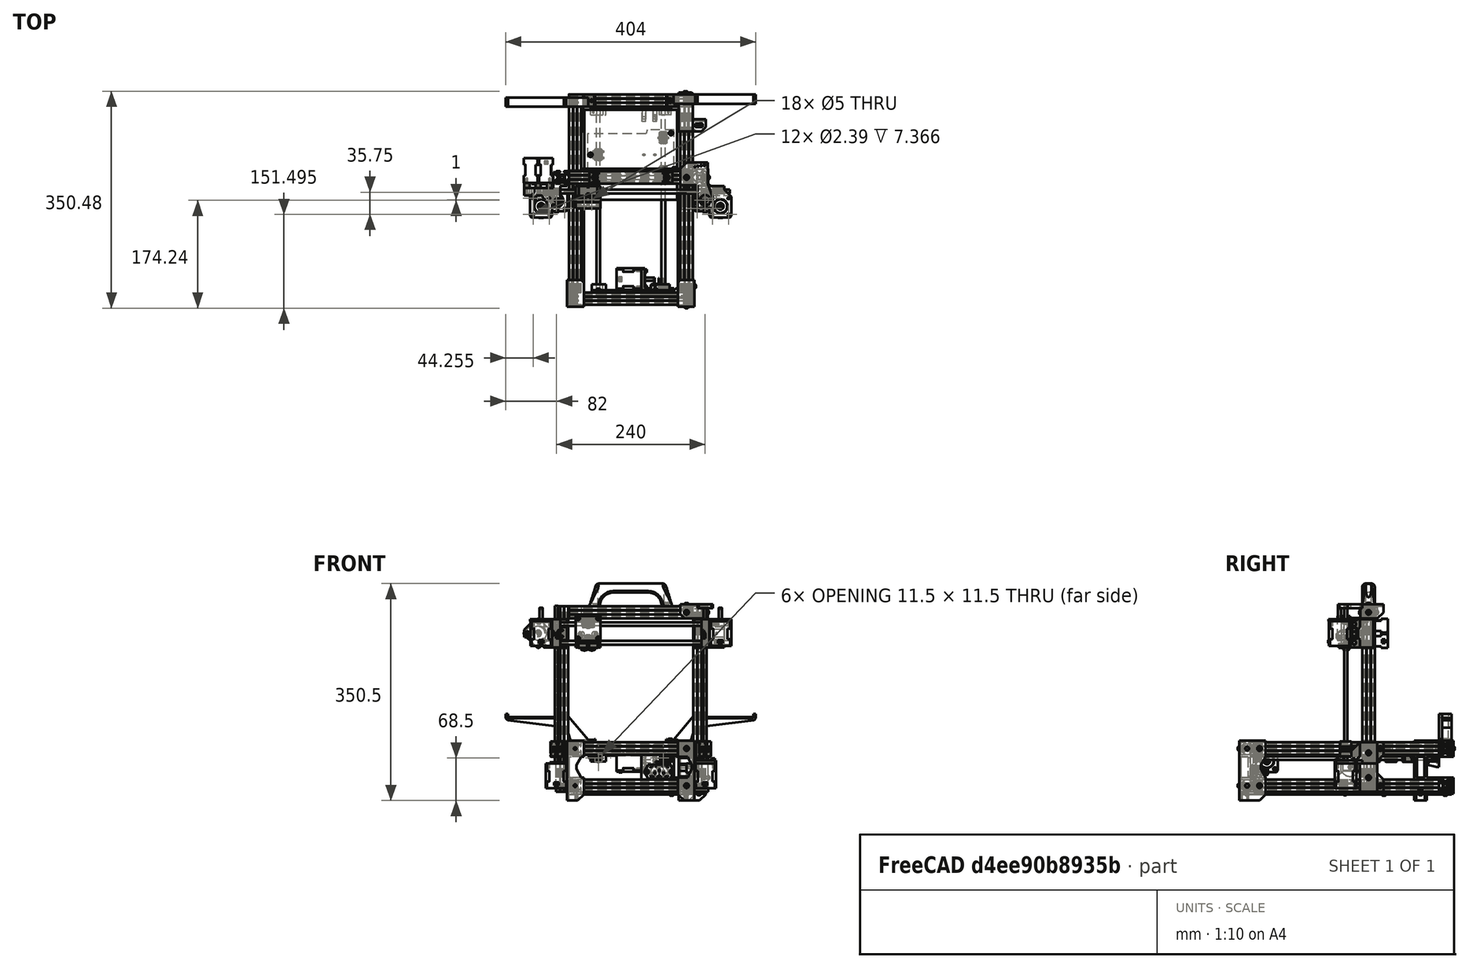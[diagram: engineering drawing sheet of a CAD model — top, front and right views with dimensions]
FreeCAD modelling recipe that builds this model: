
FCSTD DOCUMENT  (FreeCAD 0.14R3692 (Git))
Label: FoldaRap
License: CC-BY 3.0
LicenseURL: http://creativecommons.org/licenses/by/3.0/
objects: Part::Feature×136, Part::Mirroring×55, App::DocumentObjectGroup×41, Part::Compound×1
note: 192 computed .brp shape members not serialized (recipe doc carries the construction recipe); baked Part::Feature solids carry a one-line shape summary decoded from their .brp

FEATURE [Part::Feature] Part__Feature  label="foot-rear-left"
  shape: bbox 27 x 43 x 97 mm, 56 faces (baked)
FEATURE [Part::Feature] Part__Feature001  label="extrusion-p20n6b-300-bottom-left"
  Placement = pos=(10,20,10) rot=(-1,0,0;1.5708rad)
  shape: bbox 20 x 300 x 20 mm, 154 faces (baked)
FEATURE [Part::Feature] Part__Feature003  label="under-plate"
  Placement = pos=(0,0,-4) rot=(0,0,1;0rad)
  shape: bbox 200 x 340 x 4 mm, 20 faces (baked)
FEATURE [Part::Feature] Part__Feature006  label="hinge-inner-left"
  Placement = pos=(0,182,0) rot=(0,0,1;0rad)
  shape: bbox 23 x 28 x 48 mm, 30 faces (baked)
FEATURE [Part::Mirroring] Part__Mirroring001  label="hinge-inner-right"
  Base = (100,0,0)
  Normal = (1,0,0)
  Source = -> Part__Feature006
FEATURE [Part::Feature] Part__Feature009  label="nema14-stepper-motor-z-left"
  Placement = pos=(-20,169,46) rot=(0,0,-1;1.5708rad)
  shape: bbox 35.05 x 36.32 x 61.75 mm, 100 faces (baked)
FEATURE [Part::Feature] Part__Feature010  label="nema14-stepper-motor-z-right"
  Placement = pos=(220,169,46) rot=(0,0,-1;1.5708rad)
  shape: bbox 35.05 x 36.32 x 61.75 mm, 100 faces (baked)
FEATURE [Part::Feature] Part__Feature012  label="foot-rear-right"
  Placement = pos=(200,0,0) rot=(0,0,1;0rad)
  shape: bbox 33 x 43 x 97 mm, 72 faces (baked)
FEATURE [Part::Feature] Part__Feature013  label="nema14-stepper-motor-y"
  Placement = pos=(117,41.75,50) rot=(0,1,0;1.5708rad)
  shape: bbox 61.75 x 35.05 x 36.32 mm, 100 faces (baked)
FEATURE [Part::Feature] Part__Feature014  label="smooth-rod-06-300-y-left"
  Placement = pos=(47.5,20,54.5) rot=(-1,0,0;1.5708rad)
  shape: bbox 6 x 300 x 6 mm, 3 faces (baked)
FEATURE [Part::Feature] Part__Feature015  label="y-idler"
  Placement = pos=(35,316,60) rot=(0,0,1;0rad)
  shape: bbox 130 x 24 x 40 mm, 52 faces (baked)
FEATURE [Part::Feature] Part__Feature016  label="rjmp0106-linear-bearing-y-left"
  Placement = pos=(47.5,242.5,54.5) rot=(0,0,1;0rad)
  shape: bbox 12 x 19 x 12 mm, 52 faces (baked)
FEATURE [Part::Feature] Part__Feature017  label="y-carriage"
  Placement = pos=(200,282.5,58.5) rot=(0,0,1;3.14159rad)
  shape: bbox 140 x 80 x 4 mm, 174 faces (baked)
FEATURE [Part::Feature] Part__Feature018  label="bed-plate"
  Placement = pos=(25,170,76) rot=(0,0,1;0rad)
  shape: bbox 150 x 145 x 4 mm, 12 faces (baked)
FEATURE [Part::Feature] Part__Feature019  label="rjmp0106-linear-bearing-y-rear-right"
  Placement = pos=(152.5,215,54.5) rot=(0,0,1;0rad)
  shape: bbox 12 x 19 x 12 mm, 52 faces (baked)
FEATURE [Part::Feature] Part__Feature020  label="rjmp0106-linear-bearing-y-front-right"
  Placement = pos=(152.5,270,54.5) rot=(0,0,1;0rad)
  shape: bbox 12 x 19 x 12 mm, 52 faces (baked)
FEATURE [Part::Feature] Part__Feature024  label="x-carriage"
  Placement = pos=(31,183,241) rot=(0,0,1;0rad)
  shape: bbox 40 x 16 x 48 mm, 76 faces (baked)
FEATURE [Part::Feature] Part__Feature025  label="rjmp0106-linear-bearing-x-top"
  Placement = pos=(31,183,271) rot=(0,0,1;1.5708rad)
  shape: bbox 19 x 12 x 12 mm, 52 faces (baked)
FEATURE [Part::Feature] Part__Feature026  label="rjmp0106-linear-bearing-x-bottom-left"
  Placement = pos=(21,183,241) rot=(0,0,1;1.5708rad)
  shape: bbox 19 x 12 x 12 mm, 52 faces (baked)
FEATURE [Part::Feature] Part__Feature027  label="rjmp0106-linear-bearing-x-bottom-right"
  Placement = pos=(41,183,241) rot=(0,0,1;1.5708rad)
  shape: bbox 19 x 12 x 12 mm, 52 faces (baked)
FEATURE [App::DocumentObjectGroup] Grupo003  label="bearings"
  Group = -> [Part__Feature016,Part__Feature019,Part__Feature020,Part__Feature025,Part__Feature026,Part__Feature027]
FEATURE [Part::Feature] Part__Feature029  label="nema14-stepper-motor-x"
  Placement = pos=(-49.5,197,256) rot=(0.862856,0.357407,-0.357407;1.71777rad)
  shape: bbox 46.74 x 61.75 x 46.74 mm, 100 faces (baked)
FEATURE [Part::Feature] Part__Feature030  label="nema14-stepper-motor-e-right"
  Placement = pos=(244.75,159.25,276) rot=(0,0,-1;1.5708rad)
  shape: bbox 35.05 x 36.32 x 61.75 mm, 100 faces (baked)
FEATURE [Part::Feature] Part__Feature031  label="addon-handle"
  Placement = pos=(100,216,300) rot=(0,0,1;0rad)
  shape: bbox 135.3 x 20.23 x 38.29 mm, 34 faces (baked)
FEATURE [Part::Feature] Part__Feature033  label="extrusion-p20n6b-300-top-left"
  Placement = pos=(10,20,70) rot=(-1,0,0;1.5708rad)
  shape: bbox 20 x 300 x 20 mm, 154 faces (baked)
FEATURE [Part::Feature] Part__Feature034  label="extrusion-p20n6b-300-bottom-right"
  Placement = pos=(190,20,10) rot=(-1,0,0;1.5708rad)
  shape: bbox 20 x 300 x 20 mm, 154 faces (baked)
FEATURE [Part::Feature] Part__Feature034001  label="extrusion-p20n6b-300-top-right"
  Placement = pos=(190,20,70) rot=(-1,0,0;1.5708rad)
  shape: bbox 20 x 300 x 20 mm, 154 faces (baked)
FEATURE [Part::Feature] Part__Feature034002  label="extrusion-p20n6b-300-left"
  Placement = pos=(-11,206,0) rot=(0,0,1;0rad)
  shape: bbox 20 x 20 x 300 mm, 154 faces (baked)
FEATURE [Part::Feature] Part__Feature034002001  label="extrusion-p20n6b-300-right"
  Placement = pos=(211,206,0) rot=(0,0,1;0rad)
  shape: bbox 20 x 20 x 300 mm, 154 faces (baked)
FEATURE [Part::Feature] Part__Feature034002002  label="extrusion-p20n6b-200-bottom-rear"
  Placement = pos=(0,10,10) rot=(0,1,0;1.5708rad)
  shape: bbox 200 x 20 x 20 mm, 154 faces (baked)
FEATURE [Part::Feature] Part__Feature034002002001  label="extrusion-p20n6b-200-top-rear"
  Placement = pos=(0,10,70) rot=(0,1,0;1.5708rad)
  shape: bbox 200 x 20 x 20 mm, 154 faces (baked)
FEATURE [Part::Feature] Part__Feature034002002001001  label="extrusion-p20n6b-200-bottom-front"
  Placement = pos=(0,330,10) rot=(0,1,0;1.5708rad)
  shape: bbox 200 x 20 x 20 mm, 154 faces (baked)
FEATURE [Part::Feature] Part__Feature034002002001001001  label="extrusion-p20n6b-200-top-front"
  Placement = pos=(0,330,70) rot=(0,1,0;1.5708rad)
  shape: bbox 200 x 20 x 20 mm, 154 faces (baked)
FEATURE [Part::Feature] Part__Feature034002002001001001001  label="extrusion-p20n6b-200-top"
  Placement = pos=(0,206,290) rot=(0,1,0;1.5708rad)
  shape: bbox 200 x 20 x 20 mm, 154 faces (baked)
FEATURE [App::DocumentObjectGroup] Grupo001  label="extrusions"
  Group = -> [Part__Feature001,Part__Feature033,Part__Feature034,Part__Feature034001,Part__Feature034002,Part__Feature034002001,Part__Feature034002002,Part__Feature034002002001,Part__Feature034002002001001,Part__Feature034002002001001001,Part__Feature034002002001001001001]
FEATURE [Part::Feature] Part__Feature014001  label="smooth-rod-06-300-y-right"
  Placement = pos=(152.5,20,54.5) rot=(-1,0,0;1.5708rad)
  shape: bbox 6 x 300 x 6 mm, 3 faces (baked)
FEATURE [Part::Feature] Part__Feature014001001  label="smooth-rod-06-300-x-bottom"
  Placement = pos=(260,183,241) rot=(-0.57735,-0.57735,0.57735;2.0944rad)
  shape: bbox 300 x 6 x 6 mm, 3 faces (baked)
FEATURE [Part::Feature] Part__Feature014001001001  label="smooth-rod-06-300-x-top"
  Placement = pos=(260,183,271) rot=(-0.57735,-0.57735,0.57735;2.0944rad)
  shape: bbox 300 x 6 x 6 mm, 3 faces (baked)
FEATURE [Part::Feature] Part__Feature034002002001001001002  label="threaded-rod-05-230-z-left"
  Placement = pos=(-20,169,70.5) rot=(0,0,1;0rad)
  shape: bbox 5 x 5 x 230 mm, 3 faces (baked)
FEATURE [Part::Feature] Part__Feature034002002001001001002001  label="threaded-rod-05-230-z-right"
  Placement = pos=(220,169,70.5) rot=(0,0,1;0rad)
  shape: bbox 5 x 5 x 230 mm, 3 faces (baked)
FEATURE [Part::Feature] Part__Feature034002002001001001002013  label="coupling-5mm-5mm-left"
  Placement = pos=(-20,169,57) rot=(0,0,1;1.5708rad)
  shape: bbox 28.71 x 28.44 x 24.7 mm, 86 faces (baked)
FEATURE [Part::Feature] Part__Feature034002002001001001002014  label="coupling-5mm-5mm-right"
  Placement = pos=(220,169,57) rot=(0,0,1;1.5708rad)
  shape: bbox 28.71 x 28.44 x 24.7 mm, 86 faces (baked)
FEATURE [App::DocumentObjectGroup] Grupo002  label="rods"
  Group = -> [Part__Feature014,Part__Feature014001,Part__Feature014001001,Part__Feature014001001001,Part__Feature034002002001001001002,Part__Feature034002002001001001002001,Part__Feature034002002001001001002013,Part__Feature034002002001001001002014]
FEATURE [Part::Feature] Part__Feature034002002001001001002016  label="foot-front-left"
  Placement = pos=(0,340,0) rot=(0,0,1;0rad)
  shape: bbox 44 x 63 x 97 mm, 59 faces (baked)
FEATURE [Part::Mirroring] Part__Mirroring005  label="foot-front-right"
  Base = (100,0,0)
  Normal = (1,0,0)
  Source = -> Part__Feature034002002001001001002016
FEATURE [Part::Feature] Part__Feature034002002001001001002019  label="nema14-stepper-motor-e-left"
  Placement = pos=(-44.75,159.25,276) rot=(0,0,-1;1.5708rad)
  shape: bbox 35.05 x 36.32 x 61.75 mm, 100 faces (baked)
FEATURE [Part::Feature] Part__Feature034002002001001001002020  label="y-motor"
  Placement = pos=(37,20,60) rot=(0,0,1;0rad)
  shape: bbox 133 x 39.5 x 80 mm, 96 faces (baked)
FEATURE [Part::Feature] Part__Feature034002002001001001002022  label="z-motor-left"
  Placement = pos=(-20,196,46) rot=(0,0,1;0rad)
  shape: bbox 37.75 x 78.75 x 34 mm, 41 faces (baked)
FEATURE [Part::Mirroring] Part__Mirroring  label="z-motor-right"
  Base = (100,0,0)
  Normal = (1,0,0)
  Source = -> Part__Feature034002002001001001002022
FEATURE [Part::Feature] Part__Feature034002002001001001002023  label="hinge-outer-left"
  Placement = pos=(-20,196,46) rot=(0,0,1;0rad)
  shape: bbox 35 x 69 x 46 mm, 41 faces (baked)
FEATURE [Part::Mirroring] Part__Mirroring006  label="hinge-outer-right"
  Base = (100,0,0)
  Normal = (1,0,0)
  Source = -> Part__Feature034002002001001001002023
FEATURE [Part::Feature] Part__Feature034002002001001001002026  label="x-motor-spacer-left"
  Placement = pos=(0,196,233) rot=(0,0,1;0rad)
  shape: bbox 8.5 x 8 x 8.5 mm, 4 faces (baked)
FEATURE [Part::Feature] Part__Feature034002002001001001002027  label="x-motor-spacer-top"
  Placement = pos=(0,196,233) rot=(0,0,1;0rad)
  shape: bbox 8.5 x 8 x 8.5 mm, 4 faces (baked)
FEATURE [Part::Feature] Part__Feature034002002001001001002028  label="x-motor-spacer-right"
  Placement = pos=(0,196,233) rot=(0,0,1;0rad)
  shape: bbox 8.5 x 8 x 8.5 mm, 4 faces (baked)
FEATURE [Part::Feature] Part__Feature034002002001001001002030  label="connector-iec-_c14-male"
  Placement = pos=(146,17.5,32.5) rot=(0,0.707107,-0.707107;3.14159rad)
  shape: bbox 48.29 x 28.56 x 23.17 mm, 470 faces (baked)
FEATURE [App::DocumentObjectGroup] Group002  label="spacers"
  Group = -> [Part__Feature034002002001001001002028,Part__Feature034002002001001001002027,Part__Feature034002002001001001002026]
FEATURE [App::DocumentObjectGroup] Grupo004  label="motors"
  Group = -> [Part__Feature009,Part__Feature010,Part__Feature013,Part__Feature029,Part__Feature030,Part__Feature034002002001001001002019,Group002]
FEATURE [App::DocumentObjectGroup] Group  label="electrical"
  Group = -> [Part__Feature034002002001001001002030,Grupo004]
FEATURE [Part::Feature] Part__Feature034002002001001001002031  label="nut-m5-top-left"
  Placement = pos=(-20,169,272) rot=(0,0,1;0rad)
  shape: bbox 9.238 x 9.238 x 4 mm, 23 faces (baked)
FEATURE [Part::Feature] Part__Feature034002002001001001002032  label="nut-m5-bottom-left"
  Placement = pos=(-20,169,237) rot=(0,0,1;0rad)
  shape: bbox 9.238 x 9.238 x 4 mm, 23 faces (baked)
FEATURE [Part::Compound] Compound  label="m5-nut-left"
  Links = -> [Part__Feature034002002001001001002032,Part__Feature034002002001001001002031]
FEATURE [Part::Mirroring] Part__Mirroring007  label="m5-nut-right"
  Base = (100,0,0)
  Normal = (1,0,0)
  Source = -> Compound
FEATURE [Part::Feature] Part__Feature034002002001001001002034  label="bolt-m4x8-bhcs-001"
  Placement = pos=(10,-3,10) rot=(0,0,1;3.14159rad)
  shape: bbox 7.613 x 10.62 x 7.622 mm, 14 faces (baked)
FEATURE [Part::Feature] Part__Feature034002002001001001002035  label="hammer-nut-6mm-m4-001"
  Placement = pos=(10,0.5,10) rot=(0,0,1;3.14159rad)
  shape: bbox 5.9 x 4 x 11.6 mm, 18 faces (baked)
FEATURE [Part::Feature] Part__Feature034002002001001001002036  label="bolt-m4x8-bhcs-002"
  Placement = pos=(10,-3,70) rot=(0,0,1;3.14159rad)
  shape: bbox 7.613 x 10.62 x 7.622 mm, 14 faces (baked)
FEATURE [Part::Feature] Part__Feature034002002001001001002037  label="hammer-nut-6mm-m4-002"
  Placement = pos=(10,0.5,70) rot=(0,0,1;3.14159rad)
  shape: bbox 5.9 x 4 x 11.6 mm, 18 faces (baked)
FEATURE [Part::Feature] Part__Feature034002002001001001002038  label="hammer-nut-6mm-m4-003"
  Placement = pos=(0.5,30,10) rot=(0,0,1;1.5708rad)
  shape: bbox 4 x 5.9 x 11.6 mm, 18 faces (baked)
FEATURE [Part::Feature] Part__Feature034002002001001001002039  label="bolt-m4x8-bhcs-003"
  Placement = pos=(-3,30,10) rot=(0,0,1;1.5708rad)
  shape: bbox 10.62 x 7.613 x 7.622 mm, 14 faces (baked)
FEATURE [Part::Feature] Part__Feature034002002001001001002040  label="bolt-m4x8-bhcs-004"
  Placement = pos=(-3,30,70) rot=(0,0,1;1.5708rad)
  shape: bbox 10.62 x 7.613 x 7.622 mm, 14 faces (baked)
FEATURE [Part::Feature] Part__Feature034002002001001001002041  label="hammer-nut-6mm-m4-004"
  Placement = pos=(0.5,30,70) rot=(0,0,1;1.5708rad)
  shape: bbox 4 x 5.9 x 11.6 mm, 18 faces (baked)
FEATURE [Part::Mirroring] Part__Mirroring008  label="bolt-m4x8-bhcs-005"
  Base = (100,0,0)
  Normal = (1,0,0)
  Source = -> Part__Feature034002002001001001002034
FEATURE [Part::Mirroring] Part__Mirroring009  label="hammer-nut-6mm-m4-005"
  Base = (100,0,0)
  Normal = (1,0,0)
  Source = -> Part__Feature034002002001001001002035
FEATURE [Part::Mirroring] Part__Mirroring010  label="bolt-m4x8-bhcs-006"
  Base = (100,0,0)
  Normal = (1,0,0)
  Source = -> Part__Feature034002002001001001002036
FEATURE [Part::Mirroring] Part__Mirroring011  label="hammer-nut-6mm-m4-006"
  Base = (100,0,0)
  Normal = (1,0,0)
  Source = -> Part__Feature034002002001001001002037
FEATURE [Part::Mirroring] Part__Mirroring012  label="hammer-nut-6mm-m4-007"
  Base = (100,0,0)
  Normal = (1,0,0)
  Source = -> Part__Feature034002002001001001002038
FEATURE [Part::Mirroring] Part__Mirroring013  label="bolt-m4x8-bhcs-007"
  Base = (100,0,0)
  Normal = (1,0,0)
  Source = -> Part__Feature034002002001001001002039
FEATURE [Part::Mirroring] Part__Mirroring014  label="bolt-m4x8-bhcs-008"
  Base = (100,0,0)
  Normal = (1,0,0)
  Source = -> Part__Feature034002002001001001002040
FEATURE [App::DocumentObjectGroup] Group006  label="bolts-foot-rear"
  Group = -> [Part__Feature034002002001001001002034,Part__Feature034002002001001001002036,Part__Feature034002002001001001002039,Part__Feature034002002001001001002040,Part__Mirroring008,Part__Mirroring010,Part__Mirroring013,Part__Mirroring014]
FEATURE [Part::Mirroring] Part__Mirroring015  label="hammer-nut-6mm-m4-008"
  Base = (100,0,0)
  Normal = (1,0,0)
  Source = -> Part__Feature034002002001001001002041
FEATURE [App::DocumentObjectGroup] Group007  label="nuts-foot-rear"
  Group = -> [Part__Feature034002002001001001002035,Part__Feature034002002001001001002037,Part__Feature034002002001001001002038,Part__Feature034002002001001001002041,Part__Mirroring009,Part__Mirroring011,Part__Mirroring012,Part__Mirroring015]
FEATURE [Part::Feature] Part__Feature034002002001001001002042  label="bolt-m4x8-bhcs-009"
  Placement = pos=(11.5,330,-3) rot=(0,-0.707107,0.707107;3.14159rad)
  shape: bbox 7.613 x 7.622 x 10.62 mm, 14 faces (baked)
FEATURE [Part::Feature] Part__Feature034002002001001001002043  label="hammer-nut-6mm-m4-009"
  Placement = pos=(11.5,330,0.5) rot=(0,-0.707107,0.707107;3.14159rad)
  shape: bbox 5.9 x 11.6 x 4 mm, 18 faces (baked)
FEATURE [Part::Feature] Part__Feature034002002001001001002044  label="bolt-m4x8-bhcs-010"
  Placement = pos=(11.5,343,70) rot=(0,1,0;3.14159rad)
  shape: bbox 7.613 x 10.62 x 7.622 mm, 14 faces (baked)
FEATURE [Part::Feature] Part__Feature034002002001001001002045  label="hammer-nut-6mm-m4-010"
  Placement = pos=(11.5,339.5,70) rot=(0,1,0;3.14159rad)
  shape: bbox 5.9 x 4 x 11.6 mm, 18 faces (baked)
FEATURE [Part::Feature] Part__Feature034002002001001001002046  label="hammer-nut-6mm-m4-011"
  Placement = pos=(19.5,300,10) rot=(0,0,-1;1.5708rad)
  shape: bbox 4 x 5.9 x 11.6 mm, 18 faces (baked)
FEATURE [Part::Feature] Part__Feature034002002001001001002047  label="bolt-m4x8-bhcs-011"
  Placement = pos=(23,300,10) rot=(0,0,-1;1.5708rad)
  shape: bbox 10.62 x 7.613 x 7.622 mm, 14 faces (baked)
FEATURE [Part::Feature] Part__Feature034002002001001001002048  label="hammer-nut-6mm-m4-012"
  Placement = pos=(19.5,300,70) rot=(0,0,-1;1.5708rad)
  shape: bbox 4 x 5.9 x 11.6 mm, 18 faces (baked)
FEATURE [Part::Feature] Part__Feature034002002001001001002049  label="bolt-m4x8-bhcs-012"
  Placement = pos=(23,300,70) rot=(0,0,-1;1.5708rad)
  shape: bbox 10.62 x 7.613 x 7.622 mm, 14 faces (baked)
FEATURE [Part::Mirroring] Part__Mirroring016  label="bolt-m4x8-bhcs-013"
  Base = (100,0,0)
  Normal = (1,0,0)
  Source = -> Part__Feature034002002001001001002042
FEATURE [Part::Mirroring] Part__Mirroring017  label="hammer-nut-6mm-m4-013"
  Base = (100,0,0)
  Normal = (1,0,0)
  Source = -> Part__Feature034002002001001001002043
FEATURE [Part::Mirroring] Part__Mirroring018  label="bolt-m4x8-bhcs-014"
  Base = (100,0,0)
  Normal = (1,0,0)
  Source = -> Part__Feature034002002001001001002044
FEATURE [Part::Mirroring] Part__Mirroring019  label="hammer-nut-6mm-m4-014"
  Base = (100,0,0)
  Normal = (1,0,0)
  Source = -> Part__Feature034002002001001001002045
FEATURE [Part::Mirroring] Part__Mirroring020  label="hammer-nut-6mm-m4-015"
  Base = (100,0,0)
  Normal = (1,0,0)
  Source = -> Part__Feature034002002001001001002046
FEATURE [Part::Mirroring] Part__Mirroring021  label="bolt-m4x8-bhcs-015"
  Base = (100,0,0)
  Normal = (1,0,0)
  Source = -> Part__Feature034002002001001001002047
FEATURE [Part::Mirroring] Part__Mirroring022  label="hammer-nut-6mm-m4-016"
  Base = (100,0,0)
  Normal = (1,0,0)
  Source = -> Part__Feature034002002001001001002048
FEATURE [Part::Mirroring] Part__Mirroring023  label="bolt-m4x8-bhcs-016"
  Base = (100,0,0)
  Normal = (1,0,0)
  Source = -> Part__Feature034002002001001001002049
FEATURE [Part::Feature] Part__Feature034002002001001001002050  label="bolt-m4x8-bhcs-017"
  Placement = pos=(10,168,-3) rot=(-0.57735,0.57735,-0.57735;2.0944rad)
  shape: bbox 7.622 x 7.613 x 10.62 mm, 14 faces (baked)
FEATURE [Part::Feature] Part__Feature034002002001001001002051  label="hammer-nut-6mm-m4-017"
  Placement = pos=(10,168,0.5) rot=(-0.57735,0.57735,-0.57735;2.0944rad)
  shape: bbox 11.6 x 5.9 x 4 mm, 18 faces (baked)
FEATURE [Part::Mirroring] Part__Mirroring024  label="bolt-m4x8-bhcs-018"
  Base = (100,0,0)
  Normal = (1,0,0)
  Source = -> Part__Feature034002002001001001002050
FEATURE [App::DocumentObjectGroup] Group011  label="bolts-hinge-inner"
  Group = -> [Part__Feature034002002001001001002050,Part__Mirroring024]
FEATURE [Part::Mirroring] Part__Mirroring025  label="hammer-nut-6mm-m4-018"
  Base = (100,0,0)
  Normal = (1,0,0)
  Source = -> Part__Feature034002002001001001002051
FEATURE [App::DocumentObjectGroup] Group010  label="nuts-hinge-inner"
  Group = -> [Part__Feature034002002001001001002051,Part__Mirroring025]
FEATURE [Part::Feature] Part__Feature034002002001001001002052  label="bolt-m4x8-bhcs-019"
  Placement = pos=(-25,206,23) rot=(0.57735,-0.57735,0.57735;2.0944rad)
  shape: bbox 10.62 x 7.622 x 7.613 mm, 14 faces (baked)
FEATURE [Part::Feature] Part__Feature034002002001001001002053  label="hammer-nut-6mm-m4-019"
  Placement = pos=(-20.5,206,23) rot=(0.57735,-0.57735,0.57735;2.0944rad)
  shape: bbox 4 x 11.6 x 5.9 mm, 18 faces (baked)
FEATURE [Part::Mirroring] Part__Mirroring026  label="bolt-m4x8-bhcs-020"
  Base = (100,0,0)
  Normal = (1,0,0)
  Source = -> Part__Feature034002002001001001002052
FEATURE [Part::Mirroring] Part__Mirroring027  label="hammer-nut-6mm-m4-020"
  Base = (100,0,0)
  Normal = (1,0,0)
  Source = -> Part__Feature034002002001001001002053
FEATURE [Part::Feature] Part__Feature034002002001001001002054  label="hammer-nut-6mm-m4-022"
  Placement = pos=(-20.5,206,63) rot=(0.57735,-0.57735,0.57735;2.0944rad)
  shape: bbox 4 x 11.6 x 5.9 mm, 18 faces (baked)
FEATURE [Part::Mirroring] Part__Mirroring028  label="hammer-nut-6mm-m4-021"
  Base = (100,0,0)
  Normal = (1,0,0)
  Source = -> Part__Feature034002002001001001002054
FEATURE [Part::Feature] Part__Feature034002002001001001002055  label="bolt-m4x8-bhcs-021"
  Placement = pos=(-25,206,63) rot=(0.57735,-0.57735,0.57735;2.0944rad)
  shape: bbox 10.62 x 7.622 x 7.613 mm, 14 faces (baked)
FEATURE [Part::Mirroring] Part__Mirroring029  label="bolt-m4x8-bhcs-022"
  Base = (100,0,0)
  Normal = (1,0,0)
  Source = -> Part__Feature034002002001001001002055
FEATURE [Part::Feature] Part__Feature034002002001001001002056  label="hammer-nut-6mm-m4-023"
  Placement = pos=(-20.5,206,290) rot=(0.57735,-0.57735,0.57735;2.0944rad)
  shape: bbox 4 x 11.6 x 5.9 mm, 18 faces (baked)
FEATURE [Part::Feature] Part__Feature034002002001001001002057  label="bolt-m4x8-bhcs-023"
  Placement = pos=(-24,206,290) rot=(0.57735,-0.57735,0.57735;2.0944rad)
  shape: bbox 10.62 x 7.622 x 7.613 mm, 14 faces (baked)
FEATURE [Part::Feature] Part__Feature034002002001001001002058  label="hammer-nut-6mm-m4-024"
  Placement = pos=(10,196.5,290) rot=(1,0,0;3.14159rad)
  shape: bbox 5.9 x 4 x 11.6 mm, 18 faces (baked)
FEATURE [Part::Feature] Part__Feature034002002001001001002059  label="bolt-m4x8-bhcs-024"
  Placement = pos=(10,193,290) rot=(1,0,0;3.14159rad)
  shape: bbox 7.613 x 10.62 x 7.622 mm, 14 faces (baked)
FEATURE [Part::Feature] Part__Feature034002002001001001002060  label="bolt-m4x8-bhcs-025"
  Placement = pos=(10,206,303) rot=(1,0,0;1.5708rad)
  shape: bbox 7.613 x 7.622 x 10.62 mm, 14 faces (baked)
FEATURE [Part::Feature] Part__Feature034002002001001001002061  label="hammer-nut-6mm-m4-025"
  Placement = pos=(10,206,299.5) rot=(1,0,0;1.5708rad)
  shape: bbox 5.9 x 11.6 x 4 mm, 18 faces (baked)
FEATURE [Part::Mirroring] Part__Mirroring030  label="hammer-nut-6mm-m4-026"
  Base = (100,0,0)
  Normal = (1,0,0)
  Source = -> Part__Feature034002002001001001002056
FEATURE [Part::Mirroring] Part__Mirroring031  label="bolt-m4x8-bhcs-026"
  Base = (100,0,0)
  Normal = (1,0,0)
  Source = -> Part__Feature034002002001001001002057
FEATURE [Part::Mirroring] Part__Mirroring032  label="hammer-nut-6mm-m4-027"
  Base = (100,0,0)
  Normal = (1,0,0)
  Source = -> Part__Feature034002002001001001002058
FEATURE [Part::Mirroring] Part__Mirroring033  label="bolt-m4x8-bhcs-027"
  Base = (100,0,0)
  Normal = (1,0,0)
  Source = -> Part__Feature034002002001001001002059
FEATURE [Part::Mirroring] Part__Mirroring034  label="bolt-m4x8-bhcs-028"
  Base = (100,0,0)
  Normal = (1,0,0)
  Source = -> Part__Feature034002002001001001002060
FEATURE [App::DocumentObjectGroup] Group016  label="bolts-z-top"
  Group = -> [Part__Mirroring031,Part__Mirroring033,Part__Mirroring034]
FEATURE [Part::Mirroring] Part__Mirroring035  label="hammer-nut-6mm-m4-028"
  Base = (100,0,0)
  Normal = (1,0,0)
  Source = -> Part__Feature034002002001001001002061
FEATURE [App::DocumentObjectGroup] Group017  label="nuts-z-top"
  Group = -> [Part__Mirroring030,Part__Mirroring032,Part__Mirroring035]
FEATURE [Part::Feature] Part__Feature034002002001001001002062  label="bolt-m4x8-bhcs-029"
  Placement = pos=(42,206,304) rot=(1,0,0;1.5708rad)
  shape: bbox 7.613 x 7.622 x 10.62 mm, 14 faces (baked)
FEATURE [Part::Feature] Part__Feature034002002001001001002063  label="hammer-nut-6mm-m4-029"
  Placement = pos=(42,206,299.5) rot=(1,0,0;1.5708rad)
  shape: bbox 5.9 x 11.6 x 4 mm, 18 faces (baked)
FEATURE [Part::Mirroring] Part__Mirroring036  label="bolt-m4x8-bhcs-030"
  Base = (100,0,0)
  Normal = (1,0,0)
  Source = -> Part__Feature034002002001001001002062
FEATURE [App::DocumentObjectGroup] Group019  label="bolts-addon-handle"
  Group = -> [Part__Mirroring036]
FEATURE [Part::Mirroring] Part__Mirroring037  label="hammer-nut-6mm-m4-030"
  Base = (100,0,0)
  Normal = (1,0,0)
  Source = -> Part__Feature034002002001001001002063
FEATURE [App::DocumentObjectGroup] Group018  label="nuts-addon-handle"
  Group = -> [Part__Mirroring037]
FEATURE [Part::Feature] Part__Feature034002002001001001002064  label="hammer-nut-6mm-m4-031"
  Placement = pos=(146,19.5,10) rot=(0,0,1;0rad)
  shape: bbox 5.9 x 4 x 11.6 mm, 18 faces (baked)
FEATURE [Part::Feature] Part__Feature034002002001001001002065  label="bolt-m4x8-bhcs-031"
  Placement = pos=(146,24,10) rot=(0,0,1;0rad)
  shape: bbox 7.613 x 10.62 x 7.622 mm, 14 faces (baked)
FEATURE [Part::Feature] Part__Feature034002002001001001002066  label="hammer-nut-6mm-m4-032"
  Placement = pos=(47.5,19.5,70) rot=(0,0,1;0rad)
  shape: bbox 5.9 x 4 x 11.6 mm, 18 faces (baked)
FEATURE [Part::Feature] Part__Feature034002002001001001002067  label="bolt-m4x8-bhcs-032"
  Placement = pos=(47.5,24,70) rot=(0,0,1;0rad)
  shape: bbox 7.613 x 10.62 x 7.622 mm, 14 faces (baked)
FEATURE [Part::Feature] Part__Feature034002002001001001002068  label="hammer-nut-6mm-m4-033"
  Placement = pos=(140,19.5,70) rot=(0,0,1;0rad)
  shape: bbox 5.9 x 4 x 11.6 mm, 18 faces (baked)
FEATURE [Part::Feature] Part__Feature034002002001001001002069  label="bolt-m4x8-bhcs-033"
  Placement = pos=(140,24,70) rot=(0,0,1;0rad)
  shape: bbox 7.613 x 10.62 x 7.622 mm, 14 faces (baked)
FEATURE [App::DocumentObjectGroup] Group020  label="nuts-y-motor"
  Group = -> [Part__Feature034002002001001001002064,Part__Feature034002002001001001002066,Part__Feature034002002001001001002068]
FEATURE [Part::Feature] Part__Feature034002002001001001002070  label="bolt-m4x8-bhcs-034"
  Placement = pos=(47.5,316,70) rot=(1,0,0;3.14159rad)
  shape: bbox 7.613 x 10.62 x 7.622 mm, 14 faces (baked)
FEATURE [Part::Feature] Part__Feature034002002001001001002071  label="hammer-nut-6mm-m4-034"
  Placement = pos=(47.5,320.5,70) rot=(1,0,0;3.14159rad)
  shape: bbox 5.9 x 4 x 11.6 mm, 18 faces (baked)
FEATURE [Part::Feature] Part__Feature034002002001001001002072  label="bolt-m4x8-bhcs-035"
  Placement = pos=(139,316,70) rot=(1,0,0;3.14159rad)
  shape: bbox 7.613 x 10.62 x 7.622 mm, 14 faces (baked)
FEATURE [App::DocumentObjectGroup] Group023  label="bolts-y-idler"
  Group = -> [Part__Feature034002002001001001002070,Part__Feature034002002001001001002072]
FEATURE [Part::Feature] Part__Feature034002002001001001002073  label="hammer-nut-6mm-m4-035"
  Placement = pos=(139,320.5,70) rot=(1,0,0;3.14159rad)
  shape: bbox 5.9 x 4 x 11.6 mm, 18 faces (baked)
FEATURE [App::DocumentObjectGroup] Group022  label="nuts-y-idler"
  Group = -> [Part__Feature034002002001001001002071,Part__Feature034002002001001001002073]
FEATURE [Part::Feature] Part__Feature034002002001001001002074  label="hammer-nut-6mm-m4-036"
  Placement = pos=(36.5,330,79.5) rot=(0,0.707107,0.707107;3.14159rad)
  shape: bbox 5.9 x 11.6 x 4 mm, 18 faces (baked)
FEATURE [Part::Feature] Part__Feature034002002001001001002075  label="bolt-m4x8-bhcs-036"
  Placement = pos=(36.5,330,84) rot=(0,0.707107,0.707107;3.14159rad)
  shape: bbox 7.613 x 7.622 x 10.62 mm, 14 faces (baked)
FEATURE [Part::Mirroring] Part__Mirroring038  label="hammer-nut-6mm-m4-037"
  Base = (100,0,0)
  Normal = (1,0,0)
  Source = -> Part__Feature034002002001001001002074
FEATURE [App::DocumentObjectGroup] Group024  label="nuts-addon-spool-holder"
  Group = -> [Part__Mirroring038]
FEATURE [Part::Mirroring] Part__Mirroring039  label="bolt-m4x8-bhcs-037"
  Base = (100,0,0)
  Normal = (1,0,0)
  Source = -> Part__Feature034002002001001001002075
FEATURE [App::DocumentObjectGroup] Group025  label="bolts-addon-spool-holder"
  Group = -> [Part__Mirroring039]
FEATURE [Part::Feature] Part__Feature034002002001001001002076  label="hammer-nut-6mm-m4-038"
  Placement = pos=(34,10,0.5) rot=(-1,0,0;1.5708rad)
  shape: bbox 5.9 x 11.6 x 4 mm, 18 faces (baked)
FEATURE [Part::Feature] Part__Feature034002002001001001002077  label="bolt-m4x8-bhcs-038"
  Placement = pos=(34,10,-4) rot=(-1,0,0;1.5708rad)
  shape: bbox 7.613 x 7.622 x 10.62 mm, 14 faces (baked)
FEATURE [Part::Feature] Part__Feature034002002001001001002078  label="hammer-nut-6mm-m4-039"
  Placement = pos=(10,231,0.5) rot=(-0.57735,-0.57735,0.57735;2.0944rad)
  shape: bbox 11.6 x 5.9 x 4 mm, 18 faces (baked)
FEATURE [Part::Feature] Part__Feature034002002001001001002079  label="bolt-m4x8-bhcs-039"
  Placement = pos=(10,231,-4) rot=(-0.57735,-0.57735,0.57735;2.0944rad)
  shape: bbox 7.622 x 7.613 x 10.62 mm, 14 faces (baked)
FEATURE [Part::Feature] Part__Feature034002002001001001002080  label="hammer-nut-6mm-m4-040"
  Placement = pos=(34,330,0.5) rot=(-1,0,0;1.5708rad)
  shape: bbox 5.9 x 11.6 x 4 mm, 18 faces (baked)
FEATURE [Part::Feature] Part__Feature034002002001001001002081  label="bolt-m4x8-bhcs-040"
  Placement = pos=(34,330,-4) rot=(-1,0,0;1.5708rad)
  shape: bbox 7.613 x 7.622 x 10.62 mm, 14 faces (baked)
FEATURE [Part::Mirroring] Part__Mirroring040  label="hammer-nut-6mm-m4-041"
  Base = (100,0,0)
  Normal = (1,0,0)
  Source = -> Part__Feature034002002001001001002076
FEATURE [Part::Mirroring] Part__Mirroring041  label="bolt-m4x8-bhcs-041"
  Base = (100,0,0)
  Normal = (1,0,0)
  Source = -> Part__Feature034002002001001001002077
FEATURE [Part::Mirroring] Part__Mirroring042  label="hammer-nut-6mm-m4-042"
  Base = (100,0,0)
  Normal = (1,0,0)
  Source = -> Part__Feature034002002001001001002078
FEATURE [Part::Mirroring] Part__Mirroring043  label="bolt-m4x8-bhcs-042"
  Base = (100,0,0)
  Normal = (1,0,0)
  Source = -> Part__Feature034002002001001001002079
FEATURE [Part::Mirroring] Part__Mirroring044  label="hammer-nut-6mm-m4-043"
  Base = (100,0,0)
  Normal = (1,0,0)
  Source = -> Part__Feature034002002001001001002080
FEATURE [App::DocumentObjectGroup] Group026  label="nuts-under-plate"
  Group = -> [Part__Mirroring040,Part__Mirroring042,Part__Mirroring044]
FEATURE [Part::Mirroring] Part__Mirroring045  label="bolt-m4x8-bhcs-043"
  Base = (100,0,0)
  Normal = (1,0,0)
  Source = -> Part__Feature034002002001001001002081
FEATURE [App::DocumentObjectGroup] Group027  label="bolts-under-plate"
  Group = -> [Part__Mirroring041,Part__Mirroring043,Part__Mirroring045]
FEATURE [Part::Feature] Part__Feature034002002001001001002082  label="bolt-m4x8-bhcs-044"
  Placement = pos=(-10,290,-3) rot=(-0.57735,-0.57735,0.57735;2.0944rad)
  shape: bbox 7.622 x 7.613 x 10.62 mm, 14 faces (baked)
FEATURE [Part::Feature] Part__Feature034002002001001001002083  label="hammer-nut-6mm-m4-044"
  Placement = pos=(-10,290,0.5) rot=(-0.57735,-0.57735,0.57735;2.0944rad)
  shape: bbox 11.6 x 5.9 x 4 mm, 18 faces (baked)
FEATURE [Part::Mirroring] Part__Mirroring046  label="bolt-m4x8-bhcs-045"
  Base = (100,0,0)
  Normal = (1,0,0)
  Source = -> Part__Feature034002002001001001002082
FEATURE [App::DocumentObjectGroup] Group009  label="bolts-foot-front"
  Group = -> [Part__Feature034002002001001001002042,Part__Feature034002002001001001002044,Part__Feature034002002001001001002047,Part__Feature034002002001001001002049,Part__Mirroring016,Part__Mirroring018,Part__Mirroring021,Part__Mirroring023,Part__Mirroring046]
FEATURE [Part::Mirroring] Part__Mirroring047  label="hammer-nut-6mm-m4-045"
  Base = (100,0,0)
  Normal = (1,0,0)
  Source = -> Part__Feature034002002001001001002083
FEATURE [App::DocumentObjectGroup] Group008  label="nuts-foot-front"
  Group = -> [Part__Feature034002002001001001002043,Part__Feature034002002001001001002045,Part__Feature034002002001001001002046,Part__Feature034002002001001001002048,Part__Mirroring017,Part__Mirroring019,Part__Mirroring020,Part__Mirroring022,Part__Mirroring047]
FEATURE [Part::Feature] Part__Feature034002002001001001002084  label="hammer-nut-6mm-m4-046"
  Placement = pos=(0.5,225,10) rot=(0.707107,-0.707107,0;3.14159rad)
  shape: bbox 4 x 5.9 x 11.6 mm, 18 faces (baked)
FEATURE [Part::Feature] Part__Feature034002002001001001002085  label="bolt-m4x8-bhcs-046"
  Placement = pos=(-4,225,10) rot=(0.707107,-0.707107,0;3.14159rad)
  shape: bbox 10.62 x 7.613 x 7.622 mm, 14 faces (baked)
FEATURE [Part::Mirroring] Part__Mirroring048  label="hammer-nut-6mm-m4-047"
  Base = (100,0,0)
  Normal = (1,0,0)
  Source = -> Part__Feature034002002001001001002084
FEATURE [App::DocumentObjectGroup] Group012  label="nuts-hinge-outer"
  Group = -> [Part__Mirroring027,Part__Mirroring048]
FEATURE [Part::Mirroring] Part__Mirroring049  label="bolt-m4x8-bhcs-047"
  Base = (100,0,0)
  Normal = (1,0,0)
  Source = -> Part__Feature034002002001001001002085
FEATURE [App::DocumentObjectGroup] Group013  label="bolts-hinge-outer"
  Group = -> [Part__Mirroring026,Part__Mirroring049]
FEATURE [Part::Feature] Part__Feature034002002001001001002086  label="bolt-m4x8-bhcs-048"
  Placement = pos=(-4,225,70) rot=(0.707107,-0.707107,0;3.14159rad)
  shape: bbox 10.62 x 7.613 x 7.622 mm, 14 faces (baked)
FEATURE [Part::Feature] Part__Feature034002002001001001002087  label="hammer-nut-6mm-m4-048"
  Placement = pos=(0.5,225,70) rot=(0.707107,-0.707107,0;3.14159rad)
  shape: bbox 4 x 5.9 x 11.6 mm, 18 faces (baked)
FEATURE [Part::Mirroring] Part__Mirroring050  label="bolt-m4x8-bhcs-049"
  Base = (100,0,0)
  Normal = (1,0,0)
  Source = -> Part__Feature034002002001001001002086
FEATURE [Part::Mirroring] Part__Mirroring051  label="hammer-nut-6mm-m4-049"
  Base = (100,0,0)
  Normal = (1,0,0)
  Source = -> Part__Feature034002002001001001002087
FEATURE [App::DocumentObjectGroup] Group015  label="nuts-z-motor"
  Group = -> [Part__Mirroring028,Part__Mirroring051]
FEATURE [Part::Feature] Part__Feature034002002001001001002089  label="x-idler"
  Placement = pos=(200,196,233) rot=(0,0,1;0rad)
  shape: bbox 59.5 x 72.5 x 46 mm, 107 faces (baked)
FEATURE [Part::Feature] Part__Feature034002002001001001002090  label="addon-spool-holder-right"
  Placement = pos=(168,340,83) rot=(0,0,1;0rad)
  shape: bbox 145 x 20 x 46 mm, 23 faces (baked)
FEATURE [Part::Feature] Part__Feature034002002001001001002091  label="addon-spool-holder-left"
  Placement = pos=(32,320,83) rot=(0,0,1;3.14159rad)
  shape: bbox 145 x 20 x 46 mm, 23 faces (baked)
FEATURE [App::DocumentObjectGroup] Group001  label="addons"
  Group = -> [Part__Feature031,Part__Feature034002002001001001002091,Part__Feature034002002001001001002090]
FEATURE [Part::Feature] Part__Feature034002002001001001002092  label="reprap-plate"
  Placement = pos=(20,220,280) rot=(1,0,0;1.5708rad)
  shape: bbox 160 x 4 x 20 mm, 8 faces (baked)
FEATURE [App::DocumentObjectGroup] Grupo005  label="lasercuts"
  Group = -> [Part__Feature003,Part__Feature017,Part__Feature018,Part__Feature034002002001001001002092]
FEATURE [Part::Feature] Part__Feature034002002001001001002093  label="bolt-m4x8-bhcs-050"
  Placement = pos=(30,220,290) rot=(0,1,0;3.14159rad)
  shape: bbox 7.613 x 10.62 x 7.622 mm, 14 faces (baked)
FEATURE [Part::Feature] Part__Feature034002002001001001002094  label="hammer-nut-6mm-m4-050"
  Placement = pos=(30,215.5,290) rot=(0,1,0;3.14159rad)
  shape: bbox 5.9 x 4 x 11.6 mm, 18 faces (baked)
FEATURE [Part::Mirroring] Part__Mirroring052  label="bolt-m4x8-bhcs-051"
  Base = (100,0,0)
  Normal = (1,0,0)
  Source = -> Part__Feature034002002001001001002093
FEATURE [Part::Mirroring] Part__Mirroring053  label="hammer-nut-6mm-m4-051"
  Base = (100,0,0)
  Normal = (1,0,0)
  Source = -> Part__Feature034002002001001001002094
FEATURE [App::DocumentObjectGroup] Group028  label="nuts-reprap-plate"
  Group = -> [Part__Mirroring053]
FEATURE [App::DocumentObjectGroup] Group029  label="bolts-reprap-plate"
  Group = -> [Part__Mirroring052]
FEATURE [Part::Feature] Part__Feature034002002001001001002095  label="bolt-m3x20-hshcs-001"
  Placement = pos=(-67.8848,180,256) rot=(1,0,0;1.5708rad)
  shape: bbox 5.5 x 23 x 5.5 mm, 16 faces (baked)
FEATURE [Part::Feature] Part__Feature034002002001001001002096  label="bolt-m3x20-hshcs-002"
  Placement = pos=(-49.5,180,274.385) rot=(1,0,0;1.5708rad)
  shape: bbox 5.5 x 23 x 5.5 mm, 16 faces (baked)
FEATURE [Part::Feature] Part__Feature034002002001001001002097  label="bolt-m3x20-hshcs-003"
  Placement = pos=(-31.1152,180,256) rot=(1,0,0;1.5708rad)
  shape: bbox 5.5 x 23 x 5.5 mm, 16 faces (baked)
FEATURE [App::DocumentObjectGroup] Group030  label="bolts-x-motor"
  Group = -> [Part__Feature034002002001001001002095,Part__Feature034002002001001001002096,Part__Feature034002002001001001002097]
FEATURE [Part::Feature] Part__Feature034002002001001001002098  label="x-motor-e"
  Placement = pos=(0,196,233) rot=(0,0,1;0rad)
  shape: bbox 69.5 x 72.5 x 46 mm, 142 faces (baked)
FEATURE [Part::Feature] Part__Feature034002002001001001002099  label="bolt-m3x20-hshcs-004"
  Placement = pos=(18.5,174,255) rot=(1,0,0;1.5708rad)
  shape: bbox 5.5 x 23 x 5.5 mm, 16 faces (baked)
FEATURE [Part::Feature] Part__Feature034002002001001001002100  label="bolt-m3x20-hshcs-005"
  Placement = pos=(43.5,174,255) rot=(1,0,0;1.5708rad)
  shape: bbox 5.5 x 23 x 5.5 mm, 16 faces (baked)
FEATURE [Part::Feature] Part__Feature034002002001001001002101  label="bolt-m3x20-hshcs-006"
  Placement = pos=(18.5,174,278) rot=(1,0,0;1.5708rad)
  shape: bbox 5.5 x 23 x 5.5 mm, 16 faces (baked)
FEATURE [Part::Feature] Part__Feature034002002001001001002102  label="bolt-m3x20-hshcs-007"
  Placement = pos=(43.5,174,278) rot=(1,0,0;1.5708rad)
  shape: bbox 5.5 x 23 x 5.5 mm, 16 faces (baked)
FEATURE [App::DocumentObjectGroup] Group032  label="bolts-x-carriage"
  Group = -> [Part__Feature034002002001001001002099,Part__Feature034002002001001001002100,Part__Feature034002002001001001002101,Part__Feature034002002001001001002102]
FEATURE [Part::Feature] Part__Feature034002002001001001002103  label="z-top-left"
  Placement = pos=(-20,196,280) rot=(0,0,1;0rad)
  shape: bbox 52.5 x 73.5 x 23 mm, 45 faces (baked)
FEATURE [Part::Mirroring] Part__Mirroring054  label="z-top-right"
  Base = (100,0,0)
  Normal = (1,0,0)
  Source = -> Part__Feature034002002001001001002103
FEATURE [Part::Feature] Part__Feature034002002001001001002104  label="nut-m3-001"
  Placement = pos=(18.5,194.4,255) rot=(0.935113,0.250563,-0.250563;1.63783rad)
  shape: bbox 6.35 x 2.4 x 6.35 mm, 29 faces (baked)
FEATURE [Part::Feature] Part__Feature034002002001001001002105  label="nut-m3-002"
  Placement = pos=(43.5,194.4,255) rot=(0.935113,0.250563,-0.250563;1.63783rad)
  shape: bbox 6.35 x 2.4 x 6.35 mm, 29 faces (baked)
FEATURE [Part::Feature] Part__Feature034002002001001001002106  label="nut-m3-003"
  Placement = pos=(18.5,194.4,278) rot=(0.935113,0.250563,-0.250563;1.63783rad)
  shape: bbox 6.35 x 2.4 x 6.35 mm, 29 faces (baked)
FEATURE [Part::Feature] Part__Feature034002002001001001002107  label="nut-m3-004"
  Placement = pos=(43.5,194.4,278) rot=(0.935113,0.250563,-0.250563;1.63783rad)
  shape: bbox 6.35 x 2.4 x 6.35 mm, 29 faces (baked)
FEATURE [App::DocumentObjectGroup] Group031  label="nuts-x-carriage"
  Group = -> [Part__Feature034002002001001001002104,Part__Feature034002002001001001002105,Part__Feature034002002001001001002106,Part__Feature034002002001001001002107]
FEATURE [Part::Feature] Part__Feature034002002001001001002108  label="hotend-dual"
  Placement = pos=(31,170,248) rot=(0,0,1;0rad)
  shape: bbox 40 x 20 x 56 mm, 104 faces (baked)
FEATURE [Part::Feature] Part__Feature034002002001001001002109  label="bolt-m3x8-hshcs-001"
  Placement = pos=(-7,156,51) rot=(0,0,1;0rad)
  shape: bbox 5.5 x 5.5 x 11 mm, 16 faces (baked)
FEATURE [Part::Feature] Part__Feature034002002001001001002110  label="bolt-m3x8-hshcs-002"
  Placement = pos=(-33,156,51) rot=(0,0,1;0rad)
  shape: bbox 5.5 x 5.5 x 11 mm, 16 faces (baked)
FEATURE [Part::Feature] Part__Feature034002002001001001002111  label="bolt-m3x8-hshcs-003"
  Placement = pos=(-33,182,51) rot=(0,0,1;0rad)
  shape: bbox 5.5 x 5.5 x 11 mm, 16 faces (baked)
FEATURE [Part::Mirroring] Part__Mirroring055  label="bolt-m3x8-hshcs-004"
  Base = (100,0,0)
  Normal = (1,0,0)
  Source = -> Part__Feature034002002001001001002109
FEATURE [Part::Mirroring] Part__Mirroring056  label="bolt-m3x8-hshcs-005"
  Base = (100,0,0)
  Normal = (1,0,0)
  Source = -> Part__Feature034002002001001001002110
FEATURE [Part::Mirroring] Part__Mirroring057  label="bolt-m3x8-hshcs-006"
  Base = (100,0,0)
  Normal = (1,0,0)
  Source = -> Part__Feature034002002001001001002111
FEATURE [App::DocumentObjectGroup] Group014  label="bolts-z-motor"
  Group = -> [Part__Mirroring029,Part__Mirroring050,Part__Feature034002002001001001002109,Part__Feature034002002001001001002110,Part__Feature034002002001001001002111,Part__Mirroring055,Part__Mirroring056,Part__Mirroring057]
FEATURE [Part::Feature] Part__Feature034002002001001001002112  label="bolt-m3x8-hshcs-007"
  Placement = pos=(123,28.75,63) rot=(0,1,0;1.5708rad)
  shape: bbox 11 x 5.5 x 5.5 mm, 16 faces (baked)
FEATURE [Part::Feature] Part__Feature034002002001001001002113  label="bolt-m3x8-hshcs-008"
  Placement = pos=(123,54.75,63) rot=(0,1,0;1.5708rad)
  shape: bbox 11 x 5.5 x 5.5 mm, 16 faces (baked)
FEATURE [Part::Feature] Part__Feature034002002001001001002114  label="bolt-m3x8-hshcs-009"
  Placement = pos=(123,54.75,37) rot=(0,1,0;1.5708rad)
  shape: bbox 11 x 5.5 x 5.5 mm, 16 faces (baked)
FEATURE [App::DocumentObjectGroup] Group021  label="bolts-y-motor"
  Group = -> [Part__Feature034002002001001001002065,Part__Feature034002002001001001002067,Part__Feature034002002001001001002069,Part__Feature034002002001001001002112,Part__Feature034002002001001001002113,Part__Feature034002002001001001002114]
FEATURE [Part::Feature] Part__Feature034002002001001001002115  label="bolt-m3x25-hschs-001"
  Placement = pos=(35,242.5,79.75) rot=(0,0,1;0rad)
  shape: bbox 6.046 x 6.046 x 25 mm, 26 faces (baked)
FEATURE [Part::Feature] Part__Feature034002002001001001002116  label="bolt-m3x25-hschs-002"
  Placement = pos=(165,207.5,79.75) rot=(0,0,1;0rad)
  shape: bbox 6.046 x 6.046 x 25 mm, 26 faces (baked)
FEATURE [Part::Feature] Part__Feature034002002001001001002117  label="bolt-m3x25-hschs-003"
  Placement = pos=(165,277.5,79.75) rot=(0,0,1;0rad)
  shape: bbox 6.046 x 6.046 x 25 mm, 26 faces (baked)
FEATURE [App::DocumentObjectGroup] Group033  label="bolts-y-carriage"
  Group = -> [Part__Feature034002002001001001002115,Part__Feature034002002001001001002116,Part__Feature034002002001001001002117]
FEATURE [App::DocumentObjectGroup] Group005  label="bolts"
  Group = -> [Group006,Group009,Group011,Group013,Group014,Group016,Group019,Group021,Group023,Group025,Group027,Group029,Group030,Group032,Group033]
FEATURE [Part::Feature] Part__Feature034002002001001001002118  label="nyloc-nut-m3-001"
  Placement = pos=(35,242.5,58.5) rot=(1,0,0;3.14159rad)
  shape: bbox 6.35 x 6.35 x 3.86 mm, 33 faces (baked)
FEATURE [Part::Feature] Part__Feature034002002001001001002119  label="nyloc-nut-m3-002"
  Placement = pos=(165,207.5,58.5) rot=(1,0,0;3.14159rad)
  shape: bbox 6.35 x 6.35 x 3.86 mm, 33 faces (baked)
FEATURE [Part::Feature] Part__Feature034002002001001001002120  label="nyloc-nut-m3-003"
  Placement = pos=(165,277.5,58.5) rot=(1,0,0;3.14159rad)
  shape: bbox 6.35 x 6.35 x 3.86 mm, 33 faces (baked)
FEATURE [App::DocumentObjectGroup] Group034  label="nuts-y-carriage"
  Group = -> [Part__Feature034002002001001001002118,Part__Feature034002002001001001002119,Part__Feature034002002001001001002120]
FEATURE [App::DocumentObjectGroup] Group004  label="nuts"
  Group = -> [Part__Mirroring007,Group007,Group008,Group010,Group012,Group015,Group017,Group018,Group020,Group022,Group024,Group026,Group028,Group031,Group034]
FEATURE [App::DocumentObjectGroup] Group003  label="fasteners"
  Group = -> [Group004,Group005]
FEATURE [App::DocumentObjectGroup] Grupo  label="parts"
  Group = -> [Grupo001,Grupo002,Grupo003,Grupo005,Group,Group001,Group003,Part__Feature034002002001001001002108]
